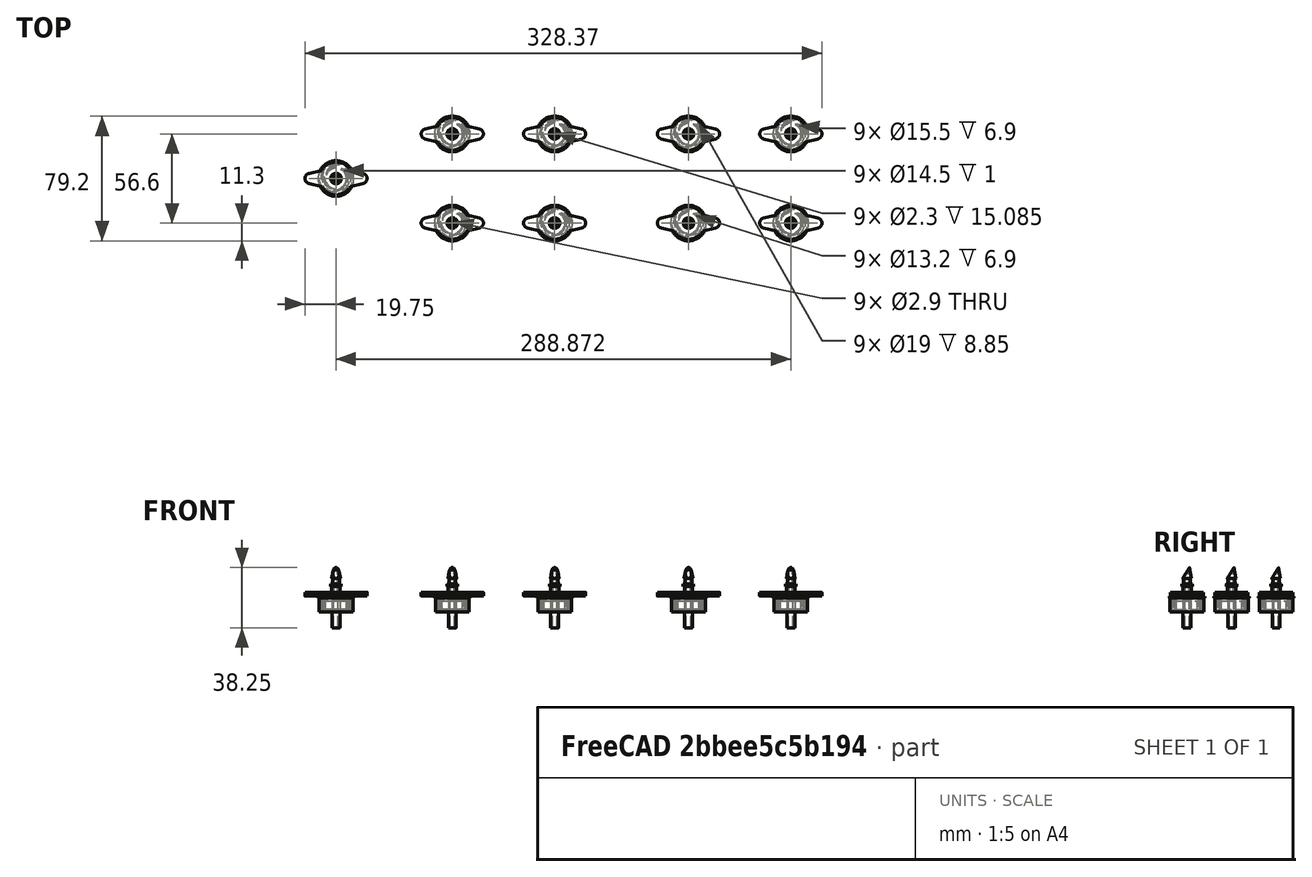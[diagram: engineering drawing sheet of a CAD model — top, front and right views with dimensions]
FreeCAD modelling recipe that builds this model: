
FCSTD DOCUMENT  (FreeCAD 1.1R38827 (Git))
Label: composit_stand3_dropper_fix_assembly
License: All rights reserved
LicenseURL: http://en.wikipedia.org/wiki/All_rights_reserved
objects: App::Link×10, PartDesign::CoordinateSystem×2, App::Part×2, Part::Compound×1, Part::FeaturePython×1, App::DocumentObjectGroup×1
note: 4 computed .brp shape members not serialized (recipe doc carries the construction recipe); baked Part::Feature solids carry a one-line shape summary decoded from their .brp
EXTERNAL_REF file=composit_stand3_dropper_fix_bottom_model.FCStd obj=Local_CS
EXTERNAL_REF file=composit_stand3_dropper_fix_bottom_model.FCStd obj=Body
EXTERNAL_REF file=composit_stand3_dropper_fix_top_model.FCStd obj=Local_CS
EXTERNAL_REF file=composit_stand3_dropper_fix_top_model.FCStd obj=Body
EXTERNAL_REF file=composit_stand3_dropper_fix_fixture_model.FCStd obj=Local_CS
EXTERNAL_REF file=composit_stand3_dropper_fix_fixture_model.FCStd obj=Body
EXTERNAL_REF file=composit_stand3_dropper_fix_cap_outer_model.FCStd obj=Local_CS
EXTERNAL_REF file=composit_stand3_dropper_fix_cap_outer_model.FCStd obj=Body
EXTERNAL_REF file=composit_stand3_dropper_fix_cap_inner_model.FCStd obj=Local_CS
EXTERNAL_REF file=composit_stand3_dropper_fix_cap_inner_model.FCStd obj=Body
EXTERNAL_REF file=composit_stand3_dropper_fix_cap_inner_model.FCStd obj=Local_CS001
EXTERNAL_REF file=composit_stand3_dropper_fix_cap_inner_model.FCStd obj=Body001
EXTERNAL_REF file=composit_stand3_dropper_fix_bottom_model.FCStd obj=Join
EXTERNAL_REF file=../dropper.FCStd obj=Body
EXTERNAL_REF file=../dropper.FCStd obj=Body001

FEATURE [PartDesign::CoordinateSystem] LCS_Origin
  AttacherType = Attacher::AttachEngine3D
FEATURE [App::Link] dropper_fix_bottom
  AttachedBy = #Local_CS
  AttachedTo = Parent Assembly#LCS_Origin
  LinkedObject = -> <external composit_stand3_dropper_fix_bottom_model.FCStd>#Body
  SolverId = Asm4EE
  expr: Placement = LCS_Origin.Placement * AttachmentOffset * composit_stand3_dropper_fix_bottom_model#Local_CS.Placement ^ -1
FEATURE [App::Link] dropper_fix_top
  AttachedBy = #Local_CS
  AttachedTo = dropper_fix_bottom#Local_CS
  LinkPlacement = pos=(0,-7e-16,6) rot=(-1,0,0;3.14159rad)
  LinkedObject = -> <external composit_stand3_dropper_fix_top_model.FCStd>#Body
  Placement = pos=(0,-7e-16,6) rot=(-1,0,0;3.14159rad)
  SolverId = Asm4EE
  expr: Placement = dropper_fix_bottom.Placement * composit_stand3_dropper_fix_bottom_model#Local_CS.Placement * AttachmentOffset * composit_stand3_dropper_fix_top_model#Local_CS.Placement ^ -1
FEATURE [App::Link] dropper_fix_fixture
  AttachedBy = #Local_CS
  AttachedTo = dropper_fix_bottom#Local_CS
  LinkPlacement = pos=(50,0,0) rot=(0,0,1;0rad)
  LinkedObject = -> <external composit_stand3_dropper_fix_fixture_model.FCStd>#Body
  Placement = pos=(50,0,0) rot=(0,0,1;0rad)
  SolverId = Asm4EE
  expr: Placement = dropper_fix_bottom.Placement * composit_stand3_dropper_fix_bottom_model#Local_CS.Placement * AttachmentOffset * composit_stand3_dropper_fix_fixture_model#Local_CS.Placement ^ -1
FEATURE [App::Link] cap_outer_dropper_fix
  AttachedBy = #Local_CS
  AttachedTo = Parent Assembly#LCS_Origin
  LinkedObject = -> <external composit_stand3_dropper_fix_cap_outer_model.FCStd>#Body
  SolverId = Asm4EE
  expr: Placement = LCS_Origin.Placement * AttachmentOffset * composit_stand3_dropper_fix_cap_outer_model#Local_CS.Placement ^ -1
FEATURE [App::Link] cap_inner_1
  AttachedBy = #Local_CS
  AttachedTo = cap_outer_dropper_fix#Local_CS
  LinkedObject = -> <external composit_stand3_dropper_fix_cap_inner_model.FCStd>#Body
  SolverId = Asm4EE
  expr: Placement = cap_outer_dropper_fix.Placement * composit_stand3_dropper_fix_cap_outer_model#Local_CS.Placement * AttachmentOffset * composit_stand3_dropper_fix_cap_inner_model#Local_CS.Placement ^ -1
FEATURE [App::Link] cap_inner_2
  AttachedBy = #Local_CS001
  AttachedTo = cap_outer_dropper_fix#Local_CS
  LinkedObject = -> <external composit_stand3_dropper_fix_cap_inner_model.FCStd>#Body001
  SolverId = Asm4EE
  expr: Placement = cap_outer_dropper_fix.Placement * composit_stand3_dropper_fix_cap_outer_model#Local_CS.Placement * AttachmentOffset * composit_stand3_dropper_fix_cap_inner_model#Local_CS001.Placement ^ -1
FEATURE [App::Link] Link001  label="Join"
  LinkedObject = -> <external composit_stand3_dropper_fix_bottom_model.FCStd>#Join
FEATURE [App::Link] Link002  label="Body"
  LinkedObject = -> <external ../dropper.FCStd>#Body
FEATURE [App::Link] Link003  label="Body001"
  LinkPlacement = pos=(0,0,2.5) rot=(0,0,1;0rad)
  LinkedObject = -> <external ../dropper.FCStd>#Body001
  Placement = pos=(0,0,2.5) rot=(0,0,1;0rad)
FEATURE [Part::Compound] Compound
  Links = -> [Link002,Link003]
  Placement = pos=(0,0,4) rot=(1,0,0;3.14159rad)
FEATURE [Part::FeaturePython] Populate  label="Populate Join with dropper"  # WARN: FeaturePython — macro-defined, semantics opaque (R4)
  Copying = 0
  ExposePlacement = false
  MarkerShape = 1
  MarkerSize = 0
  NumElements = 0
  Object = -> Compound
  OutputCompounding = 1
  PlacementsTo = -> Link001
  Referencing = 0
  Type = lattice2PopulateCopies.LatticePopulateCopies
  isLattice = 0
FEATURE [PartDesign::CoordinateSystem] base_LCS
  AttacherType = Attacher::AttachEngine3D
  AttachmentSupport = -> [XY_Plane001]
FEATURE [App::Part] Part  label="droppers"
  Group = -> [Link003,Link002,Link001,Compound,Populate,base_LCS]
  Origin = -> Origin001
FEATURE [App::DocumentObjectGroup] Parts
  Group = -> [Part]
FEATURE [App::Link] droppers  label="droppers001"
  AttachedBy = #base_LCS
  AttachedTo = Parent Assembly#LCS_Origin
  LinkedObject = -> Part
  SolverId = Asm4EE
  expr: Placement = LCS_Origin.Placement * AttachmentOffset * base_LCS.Placement ^ -1
FEATURE [App::Part] Assembly
  AssemblyType = Part::Link
  Group = -> [LCS_Origin,dropper_fix_bottom,dropper_fix_top,dropper_fix_fixture,cap_outer_dropper_fix,cap_inner_1,cap_inner_2,droppers]
  Origin = -> Origin
  Type = Assembly

RESOLVED EXTERNAL PARTS (link-assembly join: the EXTERNAL_REF files above that resolve inside this repo's crawl, each included once):
---- part ../dropper.FCStd = doc fcstd_03601a3bb068 ----
FCSTD DOCUMENT  (FreeCAD 1.1R38827 (Git))
Label: dropper
License: All rights reserved
LicenseURL: http://en.wikipedia.org/wiki/All_rights_reserved
objects: Sketcher::SketchObject×9, Part::FeaturePython×4, PartDesign::Revolution×3, PartDesign::Body×2, PartDesign::CoordinateSystem×1, Spreadsheet::Sheet×1, PartDesign::SubShapeBinder×1, PartDesign::Pad×1, PartDesign::Pocket×1, PartDesign::Groove×1, App::Part×1
note: 44 computed .brp shape members not serialized (recipe doc carries the construction recipe); baked Part::Feature solids carry a one-line shape summary decoded from their .brp

FEATURE [Sketcher::SketchObject] Sketch005
  ArcFitTolerance = 0
  AttachmentSupport = -> [YZ_Plane001]
  FullyConstrained = true
  MakeInternals = false
  MapMode = 5
  Placement = pos=(0,0,0) rot=(0.57735,0.57735,0.57735;2.0944rad)
  sketch-geometry (14):
    g0: LineSegment StartX=11.3 StartY=0 StartZ=0 EndX=11.3 EndY=1 EndZ=0
    g1: LineSegment StartX=11.3 StartY=1 StartZ=0 EndX=10.7 EndY=1 EndZ=0
    g2: LineSegment StartX=10.7 StartY=1 StartZ=0 EndX=10.7 EndY=9.9 EndZ=0
    g3: LineSegment StartX=10.7 StartY=9.9 StartZ=0 EndX=6.6 EndY=9.9 EndZ=0
    g4: LineSegment StartX=6.6 StartY=9.9 StartZ=0 EndX=6.6 EndY=3 EndZ=0
    g5: LineSegment StartX=6.6 StartY=3 StartZ=0 EndX=2.5 EndY=3 EndZ=0
    g6: LineSegment StartX=2.5 StartY=3 StartZ=0 EndX=2.5 EndY=20 EndZ=0
    g7: LineSegment StartX=2.5 StartY=20 StartZ=0 EndX=1.45 EndY=20 EndZ=0
    g8: LineSegment StartX=1.45 StartY=20 StartZ=0 EndX=1.45 EndY=2.5 EndZ=0
    g9: LineSegment StartX=1.45 StartY=2.5 StartZ=0 EndX=7 EndY=-0.6 EndZ=0
    g10: LineSegment StartX=7 StartY=-0.6 StartZ=0 EndX=7 EndY=8.85 EndZ=0
    g11: LineSegment StartX=7 StartY=8.85 StartZ=0 EndX=9.5 EndY=8.85 EndZ=0
    g12: LineSegment StartX=9.5 StartY=8.85 StartZ=0 EndX=9.5 EndY=0 EndZ=0
    g13: LineSegment StartX=9.5 StartY=0 StartZ=0 EndX=11.3 EndY=0 EndZ=0
  constraints (43):
    c: PointOnObject(g0,g-1)
    c: Vertical(g0)
    c: Coincident(g0,g1)
    c: Horizontal(g1)
    c: Coincident(g1,g2)
    c: Vertical(g2)
    c: Coincident(g2,g3)
    c: Horizontal(g3)
    c: Coincident(g3,g4)
    c: Vertical(g4)
    c: Coincident(g4,g5)
    c: Coincident(g5,g6)
    c: Vertical(g6)
    c: Coincident(g6,g7)
    c: Horizontal(g7)
    c: Coincident(g7,g8)
    c: Vertical(g8)
    c: Coincident(g8,g9)
    c: Coincident(g9,g10)
    c: Vertical(g10)
    c: Coincident(g10,g11)
    c: Horizontal(g11)
    c: Coincident(g11,g12)
    c: Vertical(g12)
    c: Coincident(g12,g13)
    c: Coincident(g13,g0)
    c: Horizontal(g13)
    c: DistanceX(g0) = 11.3  'outer_r'
    c: DistanceY(g0) = 1
    c: DistanceY(g2) = 9.9
    c: DistanceX(g1,g0) = 0.6
    c: DistanceX(g3,g2) = 4.1
    c: DistanceY(g4,g3) = 6.9
    c: DistanceX(g6) = 2.5
    c: DistanceX(g7) = 1.45
    c: DistanceY(g9,g3) = 10.5
    c: DistanceX(g12,g0) = 1.8
    c: DistanceY(g11) = 8.85
    c: DistanceX(g9) = 7
    c: DistanceY(g9,g6) = 20.6
    c: Horizontal(g5)
    c: DistanceY(g8,g5) = 0.5
    c: DistanceY(g7) = 20
FEATURE [PartDesign::Revolution] Revolution002
  Angle = 360
  Angle2 = 60
  Axis = (0,0,1)
  Base = (0,0,0)
  Placement = pos=(0,0,0) rot=(1,1,1;2.0944rad)
  Profile = -> Sketch005
  ReferenceAxis = -> Sketch005 [V_Axis]
  Reversed = true
  Suppressed = false
  Type = 0
FEATURE [Sketcher::SketchObject] Sketch006
  ArcFitTolerance = 0
  AttachmentSupport = -> [YZ_Plane001]
  FullyConstrained = true
  MakeInternals = false
  MapMode = 5
  Placement = pos=(0,0,0) rot=(0.57735,0.57735,0.57735;2.0944rad)
  expr: Constraints[27] = Sketch005.Constraints.outer_r
  expr: Constraints[28] = Sketch005.Constraints[28]
  expr: Constraints[29] = Sketch005.Constraints[29]
  expr: Constraints[30] = Sketch005.Constraints[30]
  expr: Constraints[31] = Sketch005.Constraints[31]
  expr: Constraints[32] = Sketch005.Constraints[32]
  expr: Constraints[33] = Sketch005.Constraints[33]
  expr: Constraints[34] = Sketch005.Constraints[34]
  expr: Constraints[35] = Sketch005.Constraints[35]
  expr: Constraints[36] = Sketch005.Constraints[36]
  expr: Constraints[37] = Sketch005.Constraints[37]
  expr: Constraints[38] = Sketch005.Constraints[38]
  expr: Constraints[39] = Sketch005.Constraints[39]
  expr: Constraints[41] = Sketch005.Constraints[41]
  expr: Constraints[69] = Sketch005.Constraints.outer_r
  expr: Constraints[70] = Sketch005.Constraints[28]
  expr: Constraints[71] = Sketch005.Constraints[29]
  expr: Constraints[72] = Sketch005.Constraints[30]
  expr: Constraints[73] = Sketch005.Constraints[31]
  expr: Constraints[74] = Sketch005.Constraints[32]
  expr: Constraints[75] = Sketch005.Constraints[33]
  expr: Constraints[76] = Sketch005.Constraints[34]
  expr: Constraints[77] = Sketch005.Constraints[35]
  expr: Constraints[78] = Sketch005.Constraints[36]
  expr: Constraints[79] = Sketch005.Constraints[37]
  expr: Constraints[80] = Sketch005.Constraints[38]
  expr: Constraints[81] = Sketch005.Constraints[39]
  expr: Constraints[83] = Sketch005.Constraints[41]
  sketch-geometry (32):
    g0: LineSegment [constr] StartX=11.3 StartY=0 StartZ=0 EndX=11.3 EndY=1 EndZ=0
    g1: LineSegment [constr] StartX=11.3 StartY=1 StartZ=0 EndX=10.7 EndY=1 EndZ=0
    g2: LineSegment [constr] StartX=10.7 StartY=1 StartZ=0 EndX=10.7 EndY=9.9 EndZ=0
    g3: LineSegment [constr] StartX=10.7 StartY=9.9 StartZ=0 EndX=6.6 EndY=9.9 EndZ=0
    g4: LineSegment StartX=6.6 StartY=9.9 StartZ=0 EndX=6.6 EndY=3 EndZ=0
    g5: LineSegment StartX=6.6 StartY=3 StartZ=0 EndX=2.5 EndY=3 EndZ=0
    g6: LineSegment [constr] StartX=2.5 StartY=3 StartZ=0 EndX=2.5 EndY=20 EndZ=0
    g7: LineSegment [constr] StartX=2.5 StartY=20 StartZ=0 EndX=1.45 EndY=20 EndZ=0
    g8: LineSegment [constr] StartX=1.45 StartY=20 StartZ=0 EndX=1.45 EndY=2.5 EndZ=0
    g9: LineSegment [constr] StartX=1.45 StartY=2.5 StartZ=0 EndX=7 EndY=-0.6 EndZ=0
    g10: LineSegment [constr] StartX=7 StartY=-0.6 StartZ=0 EndX=7 EndY=8.85 EndZ=0
    g11: LineSegment [constr] StartX=7 StartY=8.85 StartZ=0 EndX=9.5 EndY=8.85 EndZ=0
    g12: LineSegment [constr] StartX=9.5 StartY=8.85 StartZ=0 EndX=9.5 EndY=0 EndZ=0
    g13: LineSegment [constr] StartX=9.5 StartY=0 StartZ=0 EndX=11.3 EndY=0 EndZ=0
    g14: LineSegment [constr] StartX=11.3 StartY=0 StartZ=0 EndX=11.3 EndY=1 EndZ=0
    g15: LineSegment [constr] StartX=11.3 StartY=1 StartZ=0 EndX=10.7 EndY=1 EndZ=0
    g16: LineSegment [constr] StartX=10.7 StartY=1 StartZ=0 EndX=10.7 EndY=9.9 EndZ=0
    g17: LineSegment [constr] StartX=10.7 StartY=9.9 StartZ=0 EndX=6.6 EndY=9.9 EndZ=0
    g18: LineSegment [constr] StartX=6.6 StartY=9.9 StartZ=0 EndX=6.6 EndY=3 EndZ=0
    g19: LineSegment [constr] StartX=6.6 StartY=3 StartZ=0 EndX=2.5 EndY=3 EndZ=0
    g20: LineSegment [constr] StartX=2.5 StartY=3 StartZ=0 EndX=2.5 EndY=20 EndZ=0
    g21: LineSegment [constr] StartX=2.5 StartY=20 StartZ=0 EndX=1.45 EndY=20 EndZ=0
    g22: LineSegment [constr] StartX=1.45 StartY=20 StartZ=0 EndX=1.45 EndY=2.5 EndZ=0
    g23: LineSegment [constr] StartX=1.45 StartY=2.5 StartZ=0 EndX=7 EndY=-0.6 EndZ=0
    g24: LineSegment [constr] StartX=7 StartY=-0.6 StartZ=0 EndX=7 EndY=8.85 EndZ=0
    g25: LineSegment [constr] StartX=7 StartY=8.85 StartZ=0 EndX=9.5 EndY=8.85 EndZ=0
    g26: LineSegment [constr] StartX=9.5 StartY=8.85 StartZ=0 EndX=9.5 EndY=0 EndZ=0
    g27: LineSegment [constr] StartX=9.5 StartY=0 StartZ=0 EndX=11.3 EndY=0 EndZ=0
    g28: LineSegment StartX=2.5 StartY=3 StartZ=0 EndX=2.04763 EndY=3 EndZ=0
    g29: LineSegment StartX=2.04763 StartY=3 StartZ=0 EndX=2.04763 EndY=12.6758 EndZ=0
    g30: LineSegment StartX=2.04763 StartY=12.6758 StartZ=0 EndX=6.6 EndY=9.9 EndZ=0
    g31: GeomPoint [constr] X=2.5 Y=12.4 Z=0
  constraints (94):
    c: PointOnObject(g0,g-1)
    c: Vertical(g0)
    c: Coincident(g0,g1)
    c: Horizontal(g1)
    c: Coincident(g1,g2)
    c: Vertical(g2)
    c: Coincident(g2,g3)
    c: Horizontal(g3)
    c: Coincident(g3,g4)
    c: Vertical(g4)
    c: Coincident(g4,g5)
    c: Coincident(g5,g6)
    c: Vertical(g6)
    c: Coincident(g6,g7)
    c: Horizontal(g7)
    c: Coincident(g7,g8)
    c: Vertical(g8)
    c: Coincident(g8,g9)
    c: Coincident(g9,g10)
    c: Vertical(g10)
    c: Coincident(g10,g11)
    c: Horizontal(g11)
    c: Coincident(g11,g12)
    c: Vertical(g12)
    c: Coincident(g12,g13)
    c: Coincident(g13,g0)
    c: Horizontal(g13)
    c: DistanceX(g0) = 11.3
    c: DistanceY(g0) = 1
    c: DistanceY(g2) = 9.9
    c: DistanceX(g1,g0) = 0.6
    c: DistanceX(g3,g2) = 4.1
    c: DistanceY(g4,g3) = 6.9
    c: DistanceX(g6) = 2.5
    c: DistanceX(g7) = 1.45
    c: DistanceY(g9,g3) = 10.5
    c: DistanceX(g12,g0) = 1.8
    c: DistanceY(g11) = 8.85
    c: DistanceX(g9) = 7
    c: DistanceY(g9,g6) = 20.6
    c: Horizontal(g5)
    c: DistanceY(g8,g5) = 0.5
    c: PointOnObject(g14,g-1)
    c: Vertical(g14)
    c: Coincident(g14,g15)
    c: Horizontal(g15)
    c: Coincident(g15,g16)
    c: Vertical(g16)
    c: Coincident(g16,g17)
    c: Horizontal(g17)
    c: Coincident(g17,g18)
    c: Vertical(g18)
    c: Coincident(g18,g19)
    c: Coincident(g19,g20)
    c: Vertical(g20)
    c: Coincident(g20,g21)
    c: Horizontal(g21)
    c: Coincident(g21,g22)
    c: Vertical(g22)
    c: Coincident(g22,g23)
    c: Coincident(g23,g24)
    c: Vertical(g24)
    c: Coincident(g24,g25)
    c: Horizontal(g25)
    c: Coincident(g25,g26)
    c: Vertical(g26)
    c: Coincident(g26,g27)
    c: Coincident(g27,g14)
    c: Horizontal(g27)
    c: DistanceX(g14) = 11.3
    c: DistanceY(g14) = 1
    c: DistanceY(g16) = 9.9
    c: DistanceX(g15,g14) = 0.6
    c: DistanceX(g17,g16) = 4.1
    c: DistanceY(g18,g17) = 6.9
    c: DistanceX(g20) = 2.5
    c: DistanceX(g21) = 1.45
    c: DistanceY(g23,g17) = 10.5
    c: DistanceX(g26,g14) = 1.8
    c: DistanceY(g25) = 8.85
    c: DistanceX(g23) = 7
    c: DistanceY(g23,g20) = 20.6
    c: Horizontal(g19)
    c: DistanceY(g22,g19) = 0.5
    c: Coincident(g28,g5)
    c: Horizontal(g28)
    c: Coincident(g29,g28)
    c: Vertical(g29)
    c: Coincident(g30,g29)
    c: Coincident(g30,g4)
    c: PointOnObject(g31,g30)
    c: PointOnObject(g31,g6)
    c: DistanceY(g4,g31) = 2.5
    c: DistanceX(g29,g31) = 0.452366
FEATURE [PartDesign::Body] Body001
  AllowCompound = false
  Group = -> [Sketch005,Revolution002,Sketch006]
  Origin = -> Origin001
  Placement = pos=(0,0,2.5) rot=(0,0,1;0rad)
  Tip = -> Revolution002
FEATURE [Sketcher::SketchObject] Sketch007  label="base"
  ArcFitTolerance = 0
  FullyConstrained = true
  MakeInternals = false
  expr: .Constraints.r = Sketch005.Constraints.outer_r + 0.5 mm
  sketch-geometry (1):
    g0: Circle CenterX=0 CenterY=0 CenterZ=0 NormalX=0 NormalY=0 NormalZ=1 AngleXU=0 Radius=11.8
  constraints (2):
    c: Coincident(g0,g-1)
    c: Radius(g0) = 11.8  'r'
FEATURE [Sketcher::SketchObject] Sketch002
  ArcFitTolerance = 0
  AttachmentSupport = -> [YZ_Plane]
  FullyConstrained = true
  MakeInternals = false
  MapMode = 5
  Placement = pos=(0,0,0) rot=(0.57735,0.57735,0.57735;2.0944rad)
  expr: Constraints[18] = Sketch001.Constraints[18]
  expr: Constraints[19] = Sketch001.Constraints[19]
  expr: Constraints[20] = Sketch001.Constraints[20]
  expr: Constraints[21] = Sketch001.Constraints[21]
  expr: Constraints[22] = Sketch001.Constraints[22]
  expr: Constraints[23] = Sketch001.Constraints[23]
  expr: Constraints[24] = Sketch001.Constraints[24]
  expr: Constraints[25] = Sketch001.Constraints[25]
  expr: Constraints[27] = Sketch001.Constraints[27]
  sketch-geometry (13):
    g0: LineSegment [constr] StartX=1.15 StartY=0 StartZ=0 EndX=1.15 EndY=-18.1612 EndZ=0
    g1: LineSegment StartX=1.15 StartY=-18.1612 StartZ=0 EndX=2.765 EndY=-8.77 EndZ=0
    g2: LineSegment [constr] StartX=2.765 StartY=-8.77 StartZ=0 EndX=2.2 EndY=-8.77 EndZ=0
    g3: LineSegment [constr] StartX=2.2 StartY=-8.77 StartZ=0 EndX=2.2 EndY=-5.32 EndZ=0
    g4: LineSegment [constr] StartX=2.2 StartY=-5.32 StartZ=0 EndX=3.35 EndY=-5.32 EndZ=0
    g5: LineSegment [constr] StartX=3.35 StartY=-5.32 StartZ=0 EndX=3.35 EndY=-3.66 EndZ=0
    g6: LineSegment [constr] StartX=3.35 StartY=-3.66 StartZ=0 EndX=2.65 EndY=-3.66 EndZ=0
    g7: LineSegment [constr] StartX=2.65 StartY=-3.66 StartZ=0 EndX=2.65 EndY=0 EndZ=0
    g8: LineSegment [constr] StartX=2.65 StartY=0 StartZ=0 EndX=1.15 EndY=0 EndZ=0
    g9: GeomPoint [constr] X=-2.765 Y=-8.77 Z=0
    g10: GeomPoint [constr] X=-2.765 Y=-8.77 Z=0
    g11: LineSegment StartX=1.15 StartY=-18.1612 StartZ=0 EndX=-3.0574 EndY=-18.1612 EndZ=0
    g12: LineSegment StartX=-3.0574 StartY=-18.1612 StartZ=0 EndX=2.765 EndY=-8.77 EndZ=0
  constraints (34):
    c: PointOnObject(g0,g-1)
    c: Vertical(g0)
    c: Coincident(g0,g1)
    c: Coincident(g1,g2)
    c: Horizontal(g2)
    c: Coincident(g2,g3)
    c: Vertical(g3)
    c: Coincident(g3,g4)
    c: Horizontal(g4)
    c: Coincident(g4,g5)
    c: Vertical(g5)
    c: Coincident(g5,g6)
    c: Horizontal(g6)
    c: Coincident(g6,g7)
    c: PointOnObject(g7,g-1)
    c: Vertical(g7)
    c: Coincident(g7,g8)
    c: Coincident(g8,g0)
    c: DistanceY(g2,g3) = 3.45
    c: DistanceY(g4,g5) = 1.66
    c: DistanceY(g6,g7) = 3.66
    c: DistanceX(g2) = 2.2
    c: DistanceX(g4) = 3.35
    c: DistanceX(g0) = 1.15
    c: DistanceX(g7) = 2.65
    c: DistanceX(g1) = 2.765
    c: Symmetric(g9,g1,g-2)
    c: Distance(g9,g1) = 5.45
    c: Symmetric(g10,g1,g-2)
    c: Coincident(g11,g1)
    c: Horizontal(g11)
    c: Coincident(g12,g11)
    c: Coincident(g12,g1)
    c: Distance(g9,g12) = 4.7
FEATURE [Sketcher::SketchObject] Sketch001
  ArcFitTolerance = 0
  AttachmentSupport = -> [XZ_Plane]
  FullyConstrained = true
  MakeInternals = false
  MapMode = 5
  Placement = pos=(0,0,0) rot=(1,0,0;1.5708rad)
  sketch-geometry (10):
    g0: LineSegment StartX=1.15 StartY=0 StartZ=0 EndX=1.15 EndY=-18.1612 EndZ=0
    g1: LineSegment StartX=1.15 StartY=-18.1612 StartZ=0 EndX=2.765 EndY=-8.77 EndZ=0
    g2: LineSegment StartX=2.765 StartY=-8.77 StartZ=0 EndX=2.2 EndY=-8.77 EndZ=0
    g3: LineSegment StartX=2.2 StartY=-8.77 StartZ=0 EndX=2.2 EndY=-5.32 EndZ=0
    g4: LineSegment StartX=2.2 StartY=-5.32 StartZ=0 EndX=3.35 EndY=-5.32 EndZ=0
    g5: LineSegment StartX=3.35 StartY=-5.32 StartZ=0 EndX=3.35 EndY=-3.66 EndZ=0
    g6: LineSegment StartX=3.35 StartY=-3.66 StartZ=0 EndX=2.65 EndY=-3.66 EndZ=0
    g7: LineSegment StartX=2.65 StartY=-3.66 StartZ=0 EndX=2.65 EndY=0 EndZ=0
    g8: LineSegment StartX=2.65 StartY=0 StartZ=0 EndX=1.15 EndY=0 EndZ=0
    g9: GeomPoint [constr] X=-2.765 Y=-8.77 Z=0
  constraints (28):
    c: PointOnObject(g0,g-1)
    c: Vertical(g0)
    c: Coincident(g0,g1)
    c: Coincident(g1,g2)
    c: Horizontal(g2)
    c: Coincident(g2,g3)
    c: Vertical(g3)
    c: Coincident(g3,g4)
    c: Horizontal(g4)
    c: Coincident(g4,g5)
    c: Vertical(g5)
    c: Coincident(g5,g6)
    c: Horizontal(g6)
    c: Coincident(g6,g7)
    c: PointOnObject(g7,g-1)
    c: Vertical(g7)
    c: Coincident(g7,g8)
    c: Coincident(g8,g0)
    c: DistanceY(g2,g3) = 3.45
    c: DistanceY(g4,g5) = 1.66
    c: DistanceY(g6,g7) = 3.66
    c: DistanceX(g2) = 2.2
    c: DistanceX(g4) = 3.35
    c: DistanceX(g0) = 1.15
    c: DistanceX(g7) = 2.65
    c: DistanceX(g1) = 2.765
    c: Symmetric(g9,g1,g-2)
    c: Distance(g9,g1) = 5.45
FEATURE [Sketcher::SketchObject] Sketch  label="fix_sketch"
  ArcFitTolerance = 0
  AttachmentSupport = -> [XY_Plane]
  FullyConstrained = true
  MakeInternals = false
  MapMode = 5
  sketch-geometry (5):
    g0: ArcOfCircle CenterX=0 CenterY=0 CenterZ=0 NormalX=0 NormalY=0 NormalZ=1 AngleXU=0 Radius=10.5 StartAngle=0.496317 EndAngle=1.5708
    g1: ArcOfCircle CenterX=16.5 CenterY=0 CenterZ=0 NormalX=0 NormalY=0 NormalZ=1 AngleXU=0 Radius=3.25 StartAngle=0 EndAngle=1.34547
    g2: LineSegment StartX=17.2261 StartY=3.16784 StartZ=0 EndX=9.23309 EndY=5 EndZ=0
    g3: GeomPoint [constr] X=-19.75 Y=0 Z=0
    g4: GeomPoint [constr] X=0 Y=-10.5 Z=0
  constraints (14):
    c: PointOnObject(g0,g-2)
    c: PointOnObject(g1,g-1)
    c: PointOnObject(g1,g-1)
    c: Coincident(g2,g0)
    c: Tangent(g2,g1) = -1.5708
    c: Diameter(g0) = 21
    c: DistanceX(g1) = 19.75
    c: DistanceY(g0) = 5
    c: Diameter(g1) = 6.5
    c: Coincident(g0,g-1)
    c: Symmetric(g3,g1,g-2)
    c: DistanceX(g3,g1) = 39.5  'length'
    c: Symmetric(g4,g0,g-1)
    c: DistanceY(g4,g0) = 21  'width'
FEATURE [Sketcher::SketchObject] Sketch004
  ArcFitTolerance = 0
  AttachmentSupport = -> [YZ_Plane]
  FullyConstrained = true
  MakeInternals = false
  MapMode = 5
  Placement = pos=(0,0,0) rot=(0.57735,0.57735,0.57735;2.0944rad)
  expr: Constraints[3] = Sketch003.Constraints[9]
  sketch-geometry (6):
    g0: LineSegment StartX=7.75 StartY=10.9 StartZ=0 EndX=0 EndY=10.9 EndZ=0
    g1: LineSegment StartX=0 StartY=10.9 StartZ=0 EndX=0 EndY=1.5 EndZ=0
    g2: LineSegment StartX=0 StartY=1.5 StartZ=0 EndX=7.25 EndY=1.5 EndZ=0
    g3: LineSegment StartX=7.25 StartY=1.5 StartZ=0 EndX=7.25 EndY=2.5 EndZ=0
    g4: LineSegment StartX=7.25 StartY=2.5 StartZ=0 EndX=7.75 EndY=4 EndZ=0
    g5: LineSegment StartX=7.75 StartY=4 StartZ=0 EndX=7.75 EndY=10.9 EndZ=0
  constraints (18):
    c: Coincident(g0,g1)
    c: Horizontal(g0)
    c: Vertical(g1)
    c: DistanceY(g0) = 10.9
    c: Horizontal(g2)
    c: Coincident(g2,g3)
    c: Vertical(g3)
    c: Coincident(g3,g4)
    c: Coincident(g4,g5)
    c: Vertical(g5)
    c: Coincident(g0,g5)
    c: Coincident(g1,g2)
    c: DistanceY(g1,g0) = 9.4
    c: DistanceX(g0) = 7.75
    c: DistanceY(g2,g3) = 1
    c: DistanceY(g3,g4) = 1.5
    c: DistanceX(g2,g4) = 0.5
    c: Vertical(g1,g-1)
FEATURE [Sketcher::SketchObject] Sketch003
  ArcFitTolerance = 0
  AttachmentSupport = -> [YZ_Plane]
  FullyConstrained = true
  MakeInternals = false
  MapMode = 5
  Placement = pos=(0,0,0) rot=(0.57735,0.57735,0.57735;2.0944rad)
  sketch-geometry (4):
    g0: LineSegment StartX=0 StartY=0 StartZ=0 EndX=8.825 EndY=0 EndZ=0
    g1: LineSegment StartX=8.825 StartY=0 StartZ=0 EndX=8.825 EndY=10.9 EndZ=0
    g2: LineSegment StartX=8.825 StartY=10.9 StartZ=0 EndX=0 EndY=10.9 EndZ=0
    g3: LineSegment StartX=0 StartY=10.9 StartZ=0 EndX=0 EndY=0 EndZ=0
  constraints (11):
    c: Coincident(g0,g1)
    c: Coincident(g1,g2)
    c: Coincident(g2,g3)
    c: Coincident(g3,g0)
    c: Horizontal(g0)
    c: Horizontal(g2)
    c: Vertical(g1)
    c: Vertical(g3)
    c: Coincident(g0,g-1)
    c: DistanceY(g2) = 10.9
    c: DistanceX(g0) = 8.825
FEATURE [PartDesign::CoordinateSystem] LCS_0
  AttacherType = Attacher::AttachEngine3D
  AttachmentOffset = pos=(0,0,2.45) rot=(0,0,1;0rad)
  AttachmentSupport = -> [X_Axis002]
  MapMode = 2
  Placement = pos=(0,0,2.45) rot=(0,0,1;0rad)
FEATURE [Spreadsheet::Sheet] Spreadsheet  label="Properties"
  cells = B2(top_d)==22.6 mm; C2(bot_d)==21 mm; D2(top_height)==20 mm; E2(bot_base_height)==2.4 mm; F2(total_height)==22.4 mm; G2(total_width)==38.9 mm
FEATURE [Part::FeaturePython] Mirror  label="Mirror of Sketch"  # WARN: FeaturePython — macro-defined, semantics opaque (R4)
  ExposePlacement = false
  FlipX = true
  FlipY = false
  FlipZ = false
  MarkerShape = 1
  MarkerSize = 0
  NumElements = 0
  Object = -> Sketch
  ObjectTraversal = 0
  Type = lattice2Mirror.LatticeMirror
  isLattice = 0
FEATURE [Part::FeaturePython] Mirror001  label="Mirror001 of Mirror of Sketch"  # WARN: FeaturePython — macro-defined, semantics opaque (R4)
  ExposePlacement = false
  FlipX = false
  FlipY = true
  FlipZ = false
  MarkerShape = 1
  MarkerSize = 0
  NumElements = 0
  Object = -> Mirror
  ObjectTraversal = 0
  Type = lattice2Mirror.LatticeMirror
  isLattice = 0
FEATURE [Part::FeaturePython] Mirror002  label="Mirror002 of Mirror001 of Mirror of Sketch"  # WARN: FeaturePython — macro-defined, semantics opaque (R4)
  ExposePlacement = false
  FlipX = true
  FlipY = false
  FlipZ = false
  MarkerShape = 1
  MarkerSize = 0
  NumElements = 0
  Object = -> Mirror001
  ObjectTraversal = 0
  Type = lattice2Mirror.LatticeMirror
  isLattice = 0
FEATURE [PartDesign::SubShapeBinder] Binder
  BindCopyOnChange = 0
  BindMode = 0
  ClaimChildren = true
  Context = -> Part [Body.Binder.]
  Fuse = false
  MakeFace = true
  OffsetFill = false
  OffsetIntersection = false
  OffsetJoinType = 0
  OffsetOpenResult = false
  PartialLoad = false
  Relative = true
  Support = -> [Connect]
  _Version = 2
FEATURE [PartDesign::Pad] Pad
  Direction = (0,0,1)
  Length = 2.45
  Length2 = 10
  Profile = -> Binder
  Suppressed = false
  Type = 0
FEATURE [PartDesign::Revolution] Revolution
  Angle = 360
  Angle2 = 60
  Axis = (0,2e-16,1)
  Base = (0,0,0)
  BaseFeature = -> Pad
  Profile = -> Sketch001
  ReferenceAxis = -> Sketch001 [V_Axis]
  Reversed = true
  Suppressed = false
  Type = 0
FEATURE [PartDesign::Pocket] Pocket
  BaseFeature = -> Revolution
  Direction = (-1,0,0)
  Length = 5
  Length2 = 5
  Midplane = true
  Profile = -> Sketch002
  ReferenceAxis = -> Sketch002 [N_Axis]
  Suppressed = false
  Type = 1
FEATURE [PartDesign::Revolution] Revolution001
  Angle = 360
  Angle2 = 60
  Axis = (0,0,1)
  Base = (0,0,0)
  BaseFeature = -> Pocket
  Profile = -> Sketch003
  ReferenceAxis = -> Sketch003 [V_Axis]
  Reversed = true
  Suppressed = false
  Type = 0
FEATURE [PartDesign::Groove] Groove
  Angle = 360
  Angle2 = 60
  Axis = (0,0,1)
  Base = (0,0,0)
  BaseFeature = -> Revolution001
  Profile = -> Sketch004
  ReferenceAxis = -> Sketch004 [V_Axis]
  Suppressed = false
  Type = 0
FEATURE [Sketcher::SketchObject] Sketch008  label="feed"
  ArcFitTolerance = 0
  AttachmentSupport = -> [XY_Plane]
  FullyConstrained = true
  MakeInternals = false
  MapMode = 5
  sketch-geometry (1):
    g0: Circle CenterX=0 CenterY=0 CenterZ=0 NormalX=0 NormalY=0 NormalZ=1 AngleXU=0 Radius=4
  constraints (2):
    c: Coincident(g0,g-1)
    c: Diameter(g0) = 8
FEATURE [PartDesign::Body] Body
  AllowCompound = false
  Group = -> [Sketch,Pad,Sketch001,Revolution,Sketch002,Pocket,Sketch003,Sketch004,Revolution001,Groove,Sketch008,Binder]
  Origin = -> Origin
  Tip = -> Groove
FEATURE [App::Part] Part  label="dropper"
  Group = -> [LCS_0,Body001,Body]
  Origin = -> Origin002
FEATURE [Part::FeaturePython] Connect  label="fix"  # WARN: FeaturePython — macro-defined, semantics opaque (R4)
  Objects = -> [Sketch,Mirror002,Mirror001,Mirror]
  Tolerance = 0
---- part composit_stand3_dropper_fix_bottom_model.FCStd = doc fcstd_e59e662397be ----
FCSTD DOCUMENT  (FreeCAD 1.1R38827 (Git))
Label: composit_stand3_dropper_fix_bottom_model
License: All rights reserved
LicenseURL: http://en.wikipedia.org/wiki/All_rights_reserved
objects: Part::FeaturePython×9, PartDesign::SubShapeBinder×6, App::Link×4, PartDesign::Pad×3, PartDesign::Body×2, Part::Feature×2, Part::Mirroring×1, Part::Compound×1, Part::MultiFuse×1, PartDesign::Boolean×1, PartDesign::CoordinateSystem×1
note: 34 computed .brp shape members not serialized (recipe doc carries the construction recipe); baked Part::Feature solids carry a one-line shape summary decoded from their .brp
EXTERNAL_REF file=composit_stand3_dropper_fix_main.FCStd obj=Sketch
EXTERNAL_REF file=../dropper.FCStd obj=Sketch007
EXTERNAL_REF file=../dropper.FCStd obj=Part
EXTERNAL_REF file=composit_stand3_dropper_fix_main.FCStd obj=Populate
EXTERNAL_REF file=composit_stand3_dropper_fix_main.FCStd obj=Join
EXTERNAL_REF file=composit_stand3_main.FCStd obj=Cylinder
EXTERNAL_REF file=composit_stand3_dropper_fix_main.FCStd obj=Cylinder

FEATURE [PartDesign::SubShapeBinder] Binder
  BindCopyOnChange = 0
  BindMode = 0
  ClaimChildren = true
  Fuse = false
  MakeFace = true
  OffsetFill = false
  OffsetIntersection = false
  OffsetJoinType = 0
  OffsetOpenResult = false
  PartialLoad = false
  Relative = false
  Support = -> [<external composit_stand3_dropper_fix_main.FCStd>#Sketch]
  _Version = 2
FEATURE [Part::Mirroring] Part__Mirroring  label="Binder (Mirror #1)"
  Base = (0,0,0)
  Normal = (0,1,0)
  Source = -> Binder
FEATURE [Part::FeaturePython] Connect  # WARN: FeaturePython — macro-defined, semantics opaque (R4)
  Objects = -> [Binder,Part__Mirroring]
  Tolerance = 0
FEATURE [PartDesign::SubShapeBinder] Binder001
  BindCopyOnChange = 0
  BindMode = 0
  ClaimChildren = true
  Context = -> Body [Binder001.]
  Fuse = false
  MakeFace = true
  OffsetFill = false
  OffsetIntersection = false
  OffsetJoinType = 0
  OffsetOpenResult = false
  PartialLoad = false
  Relative = false
  Support = -> [Connect]
  _Version = 2
FEATURE [PartDesign::Pad] Pad
  Direction = (0,0,1)
  Length = 3
  Length2 = 10
  Profile = -> Binder001
  Suppressed = false
  Type = 0
FEATURE [PartDesign::SubShapeBinder] Binder002
  BindCopyOnChange = 0
  BindMode = 0
  ClaimChildren = true
  Fuse = false
  MakeFace = true
  OffsetFill = false
  OffsetIntersection = false
  OffsetJoinType = 0
  OffsetOpenResult = false
  PartialLoad = false
  Relative = false
  Support = -> [<external ../dropper.FCStd>#Sketch007]
  _Version = 2
  expr: Support = dropper#<<base>>._self
FEATURE [PartDesign::SubShapeBinder] Binder003
  BindCopyOnChange = 0
  BindMode = 0
  ClaimChildren = true
  Fuse = false
  MakeFace = true
  OffsetFill = false
  OffsetIntersection = false
  OffsetJoinType = 0
  OffsetOpenResult = false
  PartialLoad = false
  Relative = false
  Support = -> [<external ../dropper.FCStd>#Part[Body.Binder.Connect.]]
  _Version = 2
FEATURE [Part::Compound] Compound
  Links = -> [Binder002,Binder003]
FEATURE [Part::FeaturePython] FuseCompound  # WARN: FeaturePython — macro-defined, semantics opaque (R4)
  Base = -> Compound
  Refine = true
  recomputeQuota = -1
FEATURE [PartDesign::SubShapeBinder] Binder004
  BindCopyOnChange = 0
  BindMode = 0
  ClaimChildren = true
  Context = -> Body001 [Binder004.]
  Fuse = false
  MakeFace = true
  OffsetFill = false
  OffsetIntersection = false
  OffsetJoinType = 0
  OffsetOpenResult = false
  PartialLoad = false
  Relative = false
  Support = -> [Binder002]
  _Version = 2
FEATURE [PartDesign::SubShapeBinder] Binder005
  BindCopyOnChange = 0
  BindMode = 0
  ClaimChildren = true
  Context = -> Body001 [Binder005.]
  Fuse = false
  MakeFace = true
  OffsetFill = false
  OffsetIntersection = false
  OffsetJoinType = 0
  OffsetOpenResult = false
  PartialLoad = false
  Placement = pos=(0,0,1.5) rot=(0,0,1;0rad)
  Relative = false
  Support = -> [FuseCompound]
  _Version = 2
FEATURE [PartDesign::Pad] Pad001
  Direction = (0,0,1)
  Length = 10
  Length2 = 10
  Profile = -> Binder004
  Suppressed = false
  Type = 0
FEATURE [PartDesign::Pad] Pad002
  BaseFeature = -> Pad001
  Direction = (0,0,1)
  Length = 10
  Length2 = 10
  Profile = -> Binder005
  Refine = true
  Suppressed = false
  Type = 0
FEATURE [PartDesign::Body] Body001
  AllowCompound = false
  Group = -> [Binder004,Binder005,Pad001,Pad002]
  Origin = -> Origin001
  Tip = -> Pad002
FEATURE [App::Link] Link  label="Populate modules_placement_x with module_dropper"
  LinkedObject = -> <external composit_stand3_dropper_fix_main.FCStd>#Populate
FEATURE [Part::FeaturePython] Mirror  label="Mirror of Populate modules_placement_x with module_dropper"  # WARN: FeaturePython — macro-defined, semantics opaque (R4)
  ExposePlacement = false
  FlipX = false
  FlipY = true
  FlipZ = false
  MarkerShape = 1
  MarkerSize = 0
  NumElements = 4
  Object = -> Link
  ObjectTraversal = 0
  Type = lattice2Mirror.LatticeMirror
  isLattice = 1
FEATURE [Part::FeaturePython] Join  # WARN: FeaturePython — macro-defined, semantics opaque (R4)
  ExposePlacement = false
  Interleave = false
  Links = -> [Link,Mirror]
  MarkerShape = 1
  MarkerSize = 0
  NumElements = 8
  Type = lattice2JoinArrays.JoinArrays
  isLattice = 1
FEATURE [Part::FeaturePython] Populate  label="Populate Join with Body001"  # WARN: FeaturePython — macro-defined, semantics opaque (R4)
  Copying = 0
  ExposePlacement = false
  MarkerShape = 1
  MarkerSize = 0
  NumElements = 0
  Object = -> Body001
  OutputCompounding = 1
  PlacementsTo = -> Join
  Referencing = 0
  Type = lattice2PopulateCopies.LatticePopulateCopies
  isLattice = 0
FEATURE [App::Link] Link001  label="fix"
  LinkedObject = -> <external composit_stand3_dropper_fix_main.FCStd>#Join
FEATURE [App::Link] Link002  label="hole_3.4mm"
  LinkedObject = -> <external composit_stand3_main.FCStd>#Cylinder
FEATURE [Part::FeaturePython] Placment  label="top"  # WARN: FeaturePython — macro-defined, semantics opaque (R4)
  AttacherType = Attacher::AttachEngine3D
  ExposePlacement = true
  MarkerShape = 1
  MarkerSize = 20
  NumElements = 1
  Placement = pos=(0,0,6) rot=(1,0,0;3.14159rad)
  Type = lattice2AttachablePlacement.AttachablePlacement
  isLattice = 1
FEATURE [Part::FeaturePython] Populate002  label="Populate Placment with fix"  # WARN: FeaturePython — macro-defined, semantics opaque (R4)
  Copying = 0
  ExposePlacement = false
  MarkerShape = 1
  MarkerSize = 0
  NumElements = 5
  Object = -> Link001
  OutputCompounding = 0
  PlacementsTo = -> Placment
  Referencing = 0
  Type = lattice2PopulateCopies.LatticePopulateCopies
  isLattice = 1
FEATURE [Part::FeaturePython] Populate001  label="Populate fix with hole_3.4mm"  # WARN: FeaturePython — macro-defined, semantics opaque (R4)
  Copying = 0
  ExposePlacement = false
  MarkerShape = 1
  MarkerSize = 0
  NumElements = 0
  Object = -> Link002
  OutputCompounding = 1
  PlacementsTo = -> Populate002
  Referencing = 0
  Type = lattice2PopulateCopies.LatticePopulateCopies
  isLattice = 0
FEATURE [App::Link] Link003  label="feed_hole"
  LinkTransform = true
  LinkedObject = -> <external composit_stand3_dropper_fix_main.FCStd>#Cylinder
FEATURE [Part::FeaturePython] Populate003  label="Populate top with feed_hole"  # WARN: FeaturePython — macro-defined, semantics opaque (R4)
  Copying = 0
  ExposePlacement = false
  MarkerShape = 1
  MarkerSize = 0
  NumElements = 0
  Object = -> Link003
  OutputCompounding = 2
  PlacementsTo = -> Placment
  Referencing = 0
  Type = lattice2PopulateCopies.LatticePopulateCopies
  isLattice = 0
FEATURE [Part::MultiFuse] Fusion
  Shapes = -> [Populate,Populate001,Populate003]
FEATURE [PartDesign::Boolean] Boolean
  BaseFeature = -> Pad
  Group = -> [Fusion]
  Suppressed = false
  Type = 1
  UsePlacement = true
FEATURE [PartDesign::CoordinateSystem] Local_CS  label="dropper_fix_bottom_LCS"
  AttacherType = Attacher::AttachEngine3D
  AttachmentSupport = -> [XY_Plane]
  MapMode = 5
FEATURE [PartDesign::Body] Body  label="dropper_fix_bottom"
  AllowCompound = false
  Group = -> [Binder001,Pad,Boolean,Local_CS]
  Origin = -> Origin
  Tip = -> Boolean
FEATURE [Part::Feature] Body166  label="dropper_fix_bottom001"
  Placement = pos=(0,0,0) rot=(0,0,-1;1.5708rad)
  shape: bbox 345.1 x 84.2 x 3 mm, 100 faces (baked)
FEATURE [Part::Feature] Body167  label="dropper_fix_top001"
  shape: bbox 84.2 x 342.1 x 3 mm, 109 faces (baked)
---- part composit_stand3_dropper_fix_cap_inner_model.FCStd = doc fcstd_a1d9173eb1c9 ----
FCSTD DOCUMENT  (FreeCAD 1.1R38827 (Git))
Label: composit_stand3_dropper_fix_cap_inner_model
License: All rights reserved
LicenseURL: http://en.wikipedia.org/wiki/All_rights_reserved
objects: PartDesign::SubShapeBinder×3, App::Link×3, Part::FeaturePython×3, PartDesign::Body×3, Sketcher::SketchObject×2, PartDesign::FeaturePython×2, Part::MultiFuse×2, PartDesign::Boolean×2, PartDesign::CoordinateSystem×2, Part::Cylinder×1, Part::Mirroring×1
note: 27 computed .brp shape members not serialized (recipe doc carries the construction recipe); baked Part::Feature solids carry a one-line shape summary decoded from their .brp
EXTERNAL_REF file=composit_stand3_dropper_fix_cap_outer_main.FCStd obj=Spreadsheet
EXTERNAL_REF file=composit_stand3_dropper_fix_main.FCStd obj=Sketch
EXTERNAL_REF file=composit_stand3_dropper_fix_cap_outer_main.FCStd obj=Join
EXTERNAL_REF file=composit_stand3_dropper_fix_cap_outer_main.FCStd obj=Join001
EXTERNAL_REF file=composit_stand3_main.FCStd obj=Cylinder001
EXTERNAL_REF file=composit_stand3_dropper_fix_cap_outer_main.FCStd obj=Sketch

FEATURE [Sketcher::SketchObject] Sketch
  ArcFitTolerance = 0
  FullyConstrained = true
  MakeInternals = false
  expr: Constraints[10] = <<composit_stand3_dropper_fix_cap_outer_main>>#<<Properties>>.height - 3 mm
  expr: Constraints[11] = <<composit_stand3_dropper_fix_main>>#<<main_sketch>>.Constraints.width
  sketch-geometry (6):
    g0: LineSegment [constr] StartX=6 StartY=42.1 StartZ=0 EndX=6 EndY=-42.1 EndZ=0
    g1: LineSegment StartX=6 StartY=-42.1 StartZ=0 EndX=37 EndY=-42.1 EndZ=0
    g2: LineSegment StartX=37 StartY=-42.1 StartZ=0 EndX=37 EndY=42.1 EndZ=0
    g3: LineSegment StartX=37 StartY=42.1 StartZ=0 EndX=6 EndY=42.1 EndZ=0
    g4: GeomPoint [constr] X=21.5 Y=0 Z=0
    g5: LineSegment [constr] StartX=0 StartY=0 StartZ=0 EndX=6 EndY=4e-16 EndZ=0
  constraints (15):
    c: Coincident(g0,g1)
    c: Coincident(g1,g2)
    c: Coincident(g2,g3)
    c: Coincident(g3,g0)
    c: Symmetric(g2,g0,g4)
    c: Parallel(g2,g0)
    c: Parallel(g3,g1)
    c: Perpendicular(g3,g0)
    c: Coincident(g5,g-1)
    c: Symmetric(g0,g0,g5)
    c: Distance(g5,g2) = 37
    c: Distance(g2) = 84.2
    c: Perpendicular(g0,g5)
    c: Distance(g5) = 6
    c: PointOnObject(g4,g-1)
FEATURE [PartDesign::SubShapeBinder] Binder
  BindCopyOnChange = 0
  BindMode = 0
  ClaimChildren = true
  Context = -> Body [Binder.]
  Fuse = false
  MakeFace = true
  OffsetFill = false
  OffsetIntersection = false
  OffsetJoinType = 0
  OffsetOpenResult = false
  PartialLoad = false
  Placement = pos=(30,0,0) rot=(0,-1,0;1.5708rad)
  Relative = true
  Support = -> [Sketch]
  _Version = 2
FEATURE [PartDesign::SubShapeBinder] Binder001
  BindCopyOnChange = 0
  BindMode = 0
  ClaimChildren = false
  Context = -> Body001 [Binder001.]
  Fuse = false
  MakeFace = true
  OffsetFill = false
  OffsetIntersection = false
  OffsetJoinType = 0
  OffsetOpenResult = false
  PartialLoad = false
  Placement = pos=(0,0,37) rot=(0,0,1;0rad)
  Relative = true
  Support = -> [Connect]
  _Version = 2
  expr: .Placement.Base.z = <<composit_stand3_dropper_fix_cap_outer_main>>#<<Properties>>.height - 3 mm
  expr: Support = <<Connect>>._self
FEATURE [App::Link] Link  label="holes_3.4mm_placements"
  LinkClaimChild = true
  LinkTransform = true
  LinkedObject = -> <external composit_stand3_dropper_fix_cap_outer_main.FCStd>#Join
FEATURE [App::Link] Link001  label="holes_4mm_placements"
  LinkClaimChild = true
  LinkTransform = true
  LinkedObject = -> <external composit_stand3_dropper_fix_cap_outer_main.FCStd>#Join001
FEATURE [PartDesign::FeaturePython] BaseBend  # WARN: FeaturePython — macro-defined, semantics opaque (R4)
  BendSide = 1
  BendSketch = -> Binder
  MidPlane = false
  Reverse = true
  Suppressed = false
  length = 30
  radius = 0.1
  thickness = 0.3
FEATURE [App::Link] Link002  label="hole_3.4mm_rev"
  LinkClaimChild = true
  LinkTransform = true
  LinkedObject = -> <external composit_stand3_main.FCStd>#Cylinder001
FEATURE [Part::Cylinder] Cylinder  label="hole_4mm_rev"
  Angle = 360
  AttacherType = Attacher::AttachEngine3D
  FirstAngle = 0
  Height = 10
  Placement = pos=(0,0,0) rot=(1,0,0;3.14159rad)
  Radius = 2
  SecondAngle = 0
FEATURE [Part::FeaturePython] Populate  label="Populate holes_4mm_placements with hole_4mm_rev"  # WARN: FeaturePython — macro-defined, semantics opaque (R4)
  Copying = 0
  ExposePlacement = false
  MarkerShape = 1
  MarkerSize = 0
  NumElements = 0
  Object = -> Cylinder
  OutputCompounding = 1
  PlacementsTo = -> Link001
  Referencing = 0
  Type = lattice2PopulateCopies.LatticePopulateCopies
  isLattice = 0
FEATURE [Part::FeaturePython] Populate001  label="Populate holes_3.4mm_placements with hole_3.4mm_rev"  # WARN: FeaturePython — macro-defined, semantics opaque (R4)
  Copying = 0
  ExposePlacement = false
  MarkerShape = 1
  MarkerSize = 0
  NumElements = 0
  Object = -> Link002
  OutputCompounding = 1
  PlacementsTo = -> Link
  Referencing = 0
  Type = lattice2PopulateCopies.LatticePopulateCopies
  isLattice = 0
FEATURE [PartDesign::Body] Body002
  AllowCompound = false
  Origin = -> Origin002
FEATURE [Part::MultiFuse] Fusion
  Shapes = -> [Populate,Populate001]
FEATURE [PartDesign::Boolean] Boolean
  BaseFeature = -> BaseBend
  Group = -> [Fusion]
  Suppressed = false
  Type = 1
  UsePlacement = true
FEATURE [Part::MultiFuse] Fusion001
  Shapes = -> [Populate,Populate001]
FEATURE [PartDesign::FeaturePython] BaseBend001  # WARN: FeaturePython — macro-defined, semantics opaque (R4)
  BendSide = 0
  BendSketch = -> Binder001
  MidPlane = false
  Reverse = true
  Suppressed = false
  length = 70
  radius = 0.1
  thickness = 0.3
FEATURE [PartDesign::Boolean] Boolean001
  BaseFeature = -> BaseBend001
  Group = -> [Fusion001]
  Suppressed = false
  Type = 1
  UsePlacement = true
FEATURE [PartDesign::CoordinateSystem] Local_CS
  AttacherType = Attacher::AttachEngine3D
  AttachmentSupport = -> [XY_Plane]
  MapMode = 5
FEATURE [PartDesign::Body] Body  label="cap_inner_1"
  AllowCompound = false
  Group = -> [Binder,BaseBend,Boolean,Local_CS]
  Origin = -> Origin
  Tip = -> Boolean
FEATURE [PartDesign::CoordinateSystem] Local_CS001
  AttacherType = Attacher::AttachEngine3D
  AttachmentSupport = -> [XY_Plane001]
  MapMode = 5
FEATURE [PartDesign::Body] Body001  label="cap_inner_2"
  AllowCompound = false
  Group = -> [Binder001,BaseBend001,Boolean001,Local_CS001]
  Origin = -> Origin001
  Tip = -> Boolean001
FEATURE [PartDesign::SubShapeBinder] Binder002
  BindCopyOnChange = 0
  BindMode = 0
  ClaimChildren = false
  Fuse = false
  MakeFace = true
  OffsetFill = false
  OffsetIntersection = false
  OffsetJoinType = 0
  OffsetOpenResult = false
  PartialLoad = false
  Relative = true
  Support = -> [<external composit_stand3_dropper_fix_cap_outer_main.FCStd>#Sketch]
  _Version = 2
  expr: Support = composit_stand3_dropper_fix_cap_outer_main#<<main_sketch>>._self
FEATURE [Sketcher::SketchObject] Sketch001
  ArcFitTolerance = 0
  ExternalGeometry = -> [Binder002]
  FullyConstrained = true
  MakeInternals = false
  sketch-geometry (7):
    g0: LineSegment StartX=270.046 StartY=0 StartZ=0 EndX=270.046 EndY=42.1 EndZ=0
    g1: LineSegment StartX=270.046 StartY=42.1 StartZ=0 EndX=292.046 EndY=42.1 EndZ=0
    g2: LineSegment StartX=292.046 StartY=42.1 StartZ=0 EndX=348.872 EndY=14.5 EndZ=0
    g3: LineSegment StartX=348.872 StartY=14.5 StartZ=0 EndX=348.872 EndY=0 EndZ=0
    g4: LineSegment [constr] StartX=292.046 StartY=45.1 StartZ=0 EndX=292.046 EndY=42.1 EndZ=0
    g5: LineSegment [constr] StartX=292.046 StartY=42.1 StartZ=0 EndX=293.356 EndY=44.7985 EndZ=0
    g6: LineSegment [constr] StartX=348.872 StartY=14.5 StartZ=0 EndX=351.872 EndY=14.5 EndZ=0
  constraints (22):
    c: PointOnObject(g0,g-1)
    c: Vertical(g0)
    c: Coincident(g0,g1)
    c: Horizontal(g1)
    c: Coincident(g1,g2)
    c: Coincident(g2,g3)
    c: PointOnObject(g3,g-1)
    c: Vertical(g3)
    c: Coincident(g4,g1)
    c: Vertical(g4)
    c: Coincident(g4,g5)
    c: PointOnObject(g5,g-3)
    c: Coincident(g2,g6)
    c: Horizontal(g6)
    c: Vertical(g-3,g6)
    c: Perpendicular(g-3,g5)
    c: Horizontal(g4,g-3)
    c: Equal(g4,g5)
    c: Equal(g5,g6)
    c: DistanceY(g4,g4) = 3
    c: DistanceX(g1,g1) = 22
    c: Perpendicular(g5,g2)
FEATURE [Part::Mirroring] Part__Mirroring  label="Sketch001 (Mirror #1)"
  Base = (0,0,0)
  Normal = (0,1,0)
  Source = -> Sketch001
FEATURE [Part::FeaturePython] Connect  # WARN: FeaturePython — macro-defined, semantics opaque (R4)
  Objects = -> [Sketch001,Part__Mirroring]
  Tolerance = 0
---- part composit_stand3_dropper_fix_cap_outer_model.FCStd = doc fcstd_8576de4b6be2 ----
FCSTD DOCUMENT  (FreeCAD 1.1R38827 (Git))
Label: composit_stand3_dropper_fix_cap_outer_model
License: All rights reserved
LicenseURL: http://en.wikipedia.org/wiki/All_rights_reserved
objects: Part::FeaturePython×5, PartDesign::SubShapeBinder×4, Part::Mirroring×4, PartDesign::FeaturePython×3, App::Link×3, PartDesign::Body×2, Sketcher::SketchObject×2, Part::Extrusion×2, PartDesign::Pocket×1, Measure::MeasureDistance×1, App::DocumentObjectGroup×1, Part::Feature×1, Part::Cylinder×1, PartDesign::CoordinateSystem×1, Part::MultiFuse×1, PartDesign::Boolean×1
note: 36 computed .brp shape members not serialized (recipe doc carries the construction recipe); baked Part::Feature solids carry a one-line shape summary decoded from their .brp
EXTERNAL_REF file=composit_stand3_dropper_fix_cap_outer_main.FCStd obj=Sketch
EXTERNAL_REF file=composit_stand3_dropper_fix_cap_outer_main.FCStd obj=Sketch002
EXTERNAL_REF file=composit_stand3_dropper_fix_cap_outer_main.FCStd obj=Spreadsheet
EXTERNAL_REF file=composit_stand3_dropper_fix_cap_outer_main.FCStd obj=Join
EXTERNAL_REF file=composit_stand3_dropper_fix_cap_outer_main.FCStd obj=Join001
EXTERNAL_REF file=composit_stand3_main.FCStd obj=Cylinder001

FEATURE [PartDesign::SubShapeBinder] Binder
  BindCopyOnChange = 0
  BindMode = 0
  ClaimChildren = true
  Fuse = false
  MakeFace = true
  OffsetFill = false
  OffsetIntersection = false
  OffsetJoinType = 0
  OffsetOpenResult = false
  PartialLoad = false
  Relative = false
  Support = -> [<external composit_stand3_dropper_fix_cap_outer_main.FCStd>#Sketch]
  _Version = 2
FEATURE [Part::Mirroring] Part__Mirroring  label="Binder (Mirror #1)"
  Base = (0,0,0)
  Normal = (0,1,0)
  Source = -> Binder
FEATURE [Part::FeaturePython] Connect  # WARN: FeaturePython — macro-defined, semantics opaque (R4)
  Objects = -> [Binder,Part__Mirroring]
  Tolerance = 0
FEATURE [PartDesign::SubShapeBinder] Binder001
  BindCopyOnChange = 0
  BindMode = 0
  ClaimChildren = true
  Context = -> Body [Binder001.]
  Fuse = false
  MakeFace = true
  OffsetFill = false
  OffsetIntersection = false
  OffsetJoinType = 0
  OffsetOpenResult = false
  PartialLoad = false
  Relative = false
  Support = -> [Connect]
  _Version = 2
FEATURE [PartDesign::Body] Body001
  AllowCompound = false
  Origin = -> Origin001
FEATURE [PartDesign::SubShapeBinder] Binder002
  BindCopyOnChange = 0
  BindMode = 0
  ClaimChildren = true
  Fuse = false
  MakeFace = true
  OffsetFill = false
  OffsetIntersection = false
  OffsetJoinType = 0
  OffsetOpenResult = false
  PartialLoad = false
  Relative = false
  Support = -> [<external composit_stand3_dropper_fix_cap_outer_main.FCStd>#Sketch002]
  _Version = 2
FEATURE [Part::Mirroring] Part__Mirroring001  label="Binder002 (Mirror #2)"
  Base = (0,0,0)
  Normal = (0,1,0)
  Source = -> Binder002
FEATURE [Part::FeaturePython] Connect001  # WARN: FeaturePython — macro-defined, semantics opaque (R4)
  Objects = -> [Binder002,Part__Mirroring001]
  Tolerance = 0
FEATURE [PartDesign::SubShapeBinder] Binder003
  BindCopyOnChange = 0
  BindMode = 0
  ClaimChildren = false
  Context = -> Body [Binder003.]
  Fuse = false
  MakeFace = true
  OffsetFill = false
  OffsetIntersection = false
  OffsetJoinType = 0
  OffsetOpenResult = false
  PartialLoad = false
  Placement = pos=(0,0,39.6) rot=(0,0,1;0rad)
  Relative = true
  Support = -> [Connect001]
  _Version = 2
  expr: .Placement.Base.z = <<BaseBend>>.length
FEATURE [PartDesign::FeaturePython] BaseBend  # WARN: FeaturePython — macro-defined, semantics opaque (R4)
  BendSide = 1
  BendSketch = -> Binder001
  MidPlane = false
  Reverse = false
  Suppressed = false
  length = 39.6
  radius = 0.1
  thickness = 0.3
  expr: length = <<composit_stand3_dropper_fix_cap_outer_main>>#<<Properties>>.height - radius - thickness
FEATURE [PartDesign::FeaturePython] Extend  # WARN: FeaturePython — macro-defined, semantics opaque (R4)
  BaseFeature = -> BaseBend
  Offset = 0.02
  Refine = true
  Suppressed = false
  UseSubtraction = false
  baseObject = -> BaseBend [Face1]
  gap1 = 0
  gap2 = 0
  length = 0
FEATURE [PartDesign::FeaturePython] Bend  # WARN: FeaturePython — macro-defined, semantics opaque (R4)
  AutoMiter = false
  BaseFeature = -> Extend
  BendType = 0
  LengthList = [45.1]
  LengthSpec = 1
  NonperforationMaxLength = 5
  Perforate = false
  PerforationAngle = 0
  PerforationInitialLength = 5
  PerforationMaxLength = 5
  ReliefFactor = 0.7
  Suppressed = false
  UseReliefFactor = false
  angle = 90
  baseObject = -> Extend [Edge4,Edge17,Edge33,Edge107,Edge62,Edge79,Edge95]
  bendAList = [90]
  extend1 = 0
  extend2 = 0
  gap1 = 0
  gap2 = 0
  invert = false
  kfactor = 0.5
  length = 45.1
  maxExtendDist = 5
  minGap = 0.2
  minReliefGap = 1
  miterangle1 = 0
  miterangle2 = 0
  offset = 0
  radius = 0.1
  reliefType = 0
  reliefd = 1
  reliefw = 0.8
  sketchflip = false
  sketchinvert = false
  unfold = false
  expr: radius = BaseBend.radius
FEATURE [PartDesign::Pocket] Pocket
  BaseFeature = -> Bend
  Direction = (0,0,-1)
  Length = 5
  Length2 = 5
  Profile = -> Binder003
  Refine = true
  Reversed = true
  Suppressed = false
  Type = 0
FEATURE [Measure::MeasureDistance] Distance  label="Distance: 281,5882 mm"
  Distance = 281.588
  DistanceX = 281.588
  DistanceY = 0
  DistanceZ = 2.84e-14
  Element1 = -> Pocket [Edge197]
  Element2 = -> Pocket [Edge244]
  Position1 = (282.425,-0.05,40)
  Position2 = (0.837158,-0.05,40)
FEATURE [App::DocumentObjectGroup] Measurements
  Group = -> [Distance]
FEATURE [Part::Feature] Body168  label="cap_outer_material_0.30ansi002"
  Placement = pos=(0,0,0) rot=(0,0,-1;1.5708rad)
  shape: bbox 339.9 x 90.2 x 40.4 mm, 133 faces (baked)
FEATURE [App::Link] Link  label="holes_3.4mm_placements"
  LinkClaimChild = true
  LinkTransform = true
  LinkedObject = -> <external composit_stand3_dropper_fix_cap_outer_main.FCStd>#Join
FEATURE [App::Link] Link001  label="holes_4mm_placements"
  LinkClaimChild = true
  LinkTransform = true
  LinkedObject = -> <external composit_stand3_dropper_fix_cap_outer_main.FCStd>#Join001
FEATURE [App::Link] Link002  label="hole_3.4mm_rev"
  LinkTransform = true
  LinkedObject = -> <external composit_stand3_main.FCStd>#Cylinder001
FEATURE [Part::Cylinder] Cylinder  label="hole_4mm_rev"
  Angle = 360
  AttacherType = Attacher::AttachEngine3D
  FirstAngle = 0
  Height = 10
  Placement = pos=(0,0,0) rot=(1,0,0;3.14159rad)
  Radius = 2
  SecondAngle = 0
FEATURE [Part::FeaturePython] Populate  label="Populate holes_3.4mm_placements with hole_3.4mm_rev"  # WARN: FeaturePython — macro-defined, semantics opaque (R4)
  Copying = 0
  ExposePlacement = false
  MarkerShape = 1
  MarkerSize = 0
  NumElements = 0
  Object = -> Link002
  OutputCompounding = 1
  PlacementsTo = -> Link
  Referencing = 0
  Type = lattice2PopulateCopies.LatticePopulateCopies
  isLattice = 0
FEATURE [Part::FeaturePython] Populate001  label="Populate holes_4mm_placements with hole_4mm_rev"  # WARN: FeaturePython — macro-defined, semantics opaque (R4)
  Copying = 0
  ExposePlacement = false
  MarkerShape = 1
  MarkerSize = 0
  NumElements = 0
  Object = -> Cylinder
  OutputCompounding = 1
  PlacementsTo = -> Link001
  Referencing = 0
  Type = lattice2PopulateCopies.LatticePopulateCopies
  isLattice = 0
FEATURE [Sketcher::SketchObject] Sketch
  ArcFitTolerance = 0
  ExternalGeometry = -> [Body168,Connect]
  FullyConstrained = true
  MakeInternals = false
  sketch-geometry (5):
    g0: ArcOfCircle CenterX=0 CenterY=0 CenterZ=0 NormalX=0 NormalY=0 NormalZ=1 AngleXU=0 Radius=21.5 StartAngle=0 EndAngle=0.907973
    g1: ArcOfCircle CenterX=15.076 CenterY=19.3123 CenterZ=0 NormalX=0 NormalY=0 NormalZ=1 AngleXU=0 Radius=3 StartAngle=2.61799 EndAngle=4.04957
    g2: LineSegment StartX=12.4779 StartY=20.8123 StartZ=0 EndX=18.471 EndY=31.1927 EndZ=0
    g3: LineSegment StartX=18.471 StartY=31.1927 StartZ=0 EndX=18.1246 EndY=31.3927 EndZ=0
    g4: LineSegment StartX=18.1246 StartY=31.3927 StartZ=0 EndX=0 EndY=0 EndZ=0
  constraints (14):
    c: Coincident(g0,g-1)
    c: PointOnObject(g0,g-1)
    c: Tangent(g1,g0) = 1.5708
    c: Radius(g0) = 21.5
    c: Radius(g1) = 3
    c: Tangent(g1,g2) = 1.5708
    c: Coincident(g2,g3)
    c: Coincident(g3,g4)
    c: Coincident(g4,g0)
    c: Perpendicular(g3,g4)
    c: Perpendicular(g2,g3)
    c: Angle(g4) = -2.0944
    c: Distance(g4) = 36.2492
    c: Distance(g3) = 0.4
FEATURE [Part::Mirroring] Part__Mirroring002  label="Sketch (Mirror #3)"
  Base = (0,0,0)
  Normal = (0,1,0)
  Source = -> Sketch
FEATURE [Part::FeaturePython] Connect002  # WARN: FeaturePython — macro-defined, semantics opaque (R4)
  Objects = -> [Sketch,Part__Mirroring002]
  Tolerance = 0
FEATURE [Part::Extrusion] Extrude
  Base = -> Connect002
  Dir = (0,0,1)
  DirMode = 2
  FaceMakerClass = Part::FaceMakerBullseye
  FaceMakerMode = 3
  LengthFwd = 40
  LengthRev = 0
  Solid = true
  Symmetric = false
  expr: LengthFwd = <<composit_stand3_dropper_fix_cap_outer_main>>#<<Properties>>.height
FEATURE [PartDesign::CoordinateSystem] Local_CS
  AttacherType = Attacher::AttachEngine3D
  AttachmentSupport = -> [XY_Plane]
  MapMode = 5
FEATURE [Sketcher::SketchObject] Sketch001
  ArcFitTolerance = 0
  AttachmentOffset = pos=(0,0,0) rot=(0,-1,0;1.5708rad)
  AttachmentSupport = -> [Sketch]
  FullyConstrained = true
  MakeInternals = false
  MapMode = 7
  Placement = pos=(18.1246,31.3927,0) rot=(0.774597,0.447214,0.447214;1.82348rad)
  sketch-geometry (3):
    g0: LineSegment StartX=0 StartY=0 StartZ=0 EndX=3 EndY=1.865e-13 EndZ=0
    g1: LineSegment StartX=0 StartY=0 StartZ=0 EndX=1.865e-13 EndY=3 EndZ=0
    g2: ArcOfCircle CenterX=3 CenterY=3 CenterZ=0 NormalX=0 NormalY=0 NormalZ=1 AngleXU=0 Radius=3 StartAngle=3.14159 EndAngle=4.71239
  constraints (7):
    c: Coincident(g-1,g0)
    c: PointOnObject(g0,g-1)
    c: Coincident(g0,g1)
    c: PointOnObject(g1,g-2)
    c: Tangent(g2,g1) = 1.5708
    c: Tangent(g2,g0) = -1.5708
    c: Radius(g2) = 3
FEATURE [Part::Extrusion] Extrude001
  Base = -> Sketch001
  Dir = (0.866025,-0.5,1e-16)
  DirMode = 2
  FaceMakerClass = Part::FaceMakerBullseye
  FaceMakerMode = 3
  LengthFwd = 10
  LengthRev = 0
  Solid = true
  Symmetric = false
FEATURE [Part::Mirroring] Part__Mirroring003  label="Extrude001 (Mirror #4)"
  Base = (0,0,0)
  Normal = (0,1,0)
  Source = -> Extrude001
FEATURE [Part::MultiFuse] Fusion
  Shapes = -> [Populate,Populate001,Extrude,Extrude001,Part__Mirroring003]
FEATURE [PartDesign::Boolean] Boolean
  BaseFeature = -> Pocket
  Group = -> [Fusion]
  Suppressed = false
  Type = 1
  UsePlacement = true
FEATURE [PartDesign::Body] Body  label="cap_outer_dropper_fix"
  AllowCompound = false
  Group = -> [Binder001,Binder003,BaseBend,Extend,Bend,Pocket,Boolean,Local_CS]
  Origin = -> Origin
  Tip = -> Boolean
---- part composit_stand3_dropper_fix_fixture_model.FCStd = doc fcstd_42cb5ebbac59 ----
FCSTD DOCUMENT  (FreeCAD 1.1R38827 (Git))
Label: composit_stand3_dropper_fix_fixture_model
License: All rights reserved
LicenseURL: http://en.wikipedia.org/wiki/All_rights_reserved
objects: App::Link×4, Part::FeaturePython×3, PartDesign::SubShapeBinder×2, PartDesign::Body×2, PartDesign::FeaturePython×1, Part::MultiFuse×1, PartDesign::Boolean×1, PartDesign::CoordinateSystem×1
note: 13 computed .brp shape members not serialized (recipe doc carries the construction recipe); baked Part::Feature solids carry a one-line shape summary decoded from their .brp
EXTERNAL_REF file=composit_stand3_dropper_fix_fixture_main.FCStd obj=Sketch
EXTERNAL_REF file=composit_stand3_dropper_fix_fixture_main.FCStd obj=Placment
EXTERNAL_REF file=composit_stand3_main.FCStd obj=Cylinder
EXTERNAL_REF file=composit_stand3_dropper_fix_fixture_main.FCStd obj=Join
EXTERNAL_REF file=composit_stand3_dropper_fix_main.FCStd obj=Join

FEATURE [PartDesign::SubShapeBinder] Binder
  BindCopyOnChange = 0
  BindMode = 0
  ClaimChildren = true
  Fuse = false
  MakeFace = true
  OffsetFill = false
  OffsetIntersection = false
  OffsetJoinType = 0
  OffsetOpenResult = false
  PartialLoad = false
  Placement = pos=(0,0,0) rot=(0.57735,0.57735,0.57735;2.0944rad)
  Relative = false
  Support = -> [<external composit_stand3_dropper_fix_fixture_main.FCStd>#Sketch]
  _Version = 2
  expr: Placement = Support[0][0].Placement
FEATURE [PartDesign::SubShapeBinder] Binder001
  BindCopyOnChange = 0
  BindMode = 0
  ClaimChildren = true
  Context = -> Body [Binder001.]
  Fuse = false
  MakeFace = true
  OffsetFill = false
  OffsetIntersection = false
  OffsetJoinType = 0
  OffsetOpenResult = false
  PartialLoad = false
  Placement = pos=(0,0,0) rot=(0.57735,0.57735,0.57735;2.0944rad)
  Relative = false
  Support = -> [Binder]
  _Version = 2
  expr: Placement = Support[0][0].Placement
FEATURE [PartDesign::FeaturePython] BaseBend  # WARN: FeaturePython — macro-defined, semantics opaque (R4)
  BendSide = 1
  BendSketch = -> Binder001
  MidPlane = false
  Reverse = false
  Suppressed = false
  length = 100
  radius = 0.1
  thickness = 0.3
FEATURE [App::Link] Link  label="Placment"
  LinkTransform = true
  LinkedObject = -> <external composit_stand3_dropper_fix_fixture_main.FCStd>#Placment
FEATURE [App::Link] Link001  label="hole_3.4mm"
  LinkedObject = -> <external composit_stand3_main.FCStd>#Cylinder
FEATURE [App::Link] Link002  label="Join"
  LinkedObject = -> <external composit_stand3_dropper_fix_fixture_main.FCStd>#Join
FEATURE [PartDesign::Body] Body001
  AllowCompound = false
  Origin = -> Origin001
FEATURE [App::Link] Link003  label="fix"
  LinkedObject = -> <external composit_stand3_dropper_fix_main.FCStd>#Join
FEATURE [Part::FeaturePython] Populate001  label="Populate Placment with fix"  # WARN: FeaturePython — macro-defined, semantics opaque (R4)
  Copying = 0
  ExposePlacement = false
  MarkerShape = 1
  MarkerSize = 0
  NumElements = 5
  Object = -> Link003
  OutputCompounding = 0
  PlacementsTo = -> Link
  Referencing = 0
  Type = lattice2PopulateCopies.LatticePopulateCopies
  isLattice = 1
FEATURE [Part::FeaturePython] Join  label="Join001"  # WARN: FeaturePython — macro-defined, semantics opaque (R4)
  ExposePlacement = false
  Interleave = false
  Links = -> [Link002,Populate001]
  MarkerShape = 1
  MarkerSize = 0
  NumElements = 15
  Type = lattice2JoinArrays.JoinArrays
  isLattice = 1
FEATURE [Part::FeaturePython] Populate  label="Populate Join with hole_3.4mm"  # WARN: FeaturePython — macro-defined, semantics opaque (R4)
  Copying = 0
  ExposePlacement = false
  MarkerShape = 1
  MarkerSize = 0
  NumElements = 0
  Object = -> Link001
  OutputCompounding = 1
  PlacementsTo = -> Join
  Referencing = 0
  Type = lattice2PopulateCopies.LatticePopulateCopies
  isLattice = 0
FEATURE [Part::MultiFuse] Fusion
  Shapes = -> [Populate]
FEATURE [PartDesign::Boolean] Boolean
  BaseFeature = -> BaseBend
  Group = -> [Fusion]
  Suppressed = false
  Type = 1
  UsePlacement = true
FEATURE [PartDesign::CoordinateSystem] Local_CS
  AttacherType = Attacher::AttachEngine3D
  AttachmentOffset = pos=(-50,0,0) rot=(0,0,1;0rad)
  AttachmentSupport = -> [XY_Plane]
  MapMode = 5
  Placement = pos=(-50,0,0) rot=(0,0,1;0rad)
  expr: .AttachmentOffset.Base.x = <<Placment>>.LinkedObject.Placement.Base.x
FEATURE [PartDesign::Body] Body  label="dropper_fix_fixture"
  AllowCompound = false
  Group = -> [Binder001,BaseBend,Boolean,Local_CS]
  Origin = -> Origin
  Tip = -> Boolean
---- part composit_stand3_dropper_fix_top_model.FCStd = doc fcstd_5f1bdb20550e ----
FCSTD DOCUMENT  (FreeCAD 1.1R38827 (Git))
Label: composit_stand3_dropper_fix_top_model
License: All rights reserved
LicenseURL: http://en.wikipedia.org/wiki/All_rights_reserved
objects: PartDesign::SubShapeBinder×7, Part::FeaturePython×6, App::Link×4, PartDesign::Pad×3, PartDesign::Body×2, Part::Mirroring×1, Part::Compound×1, Part::MultiFuse×1, PartDesign::Boolean×1, PartDesign::CoordinateSystem×1
note: 30 computed .brp shape members not serialized (recipe doc carries the construction recipe); baked Part::Feature solids carry a one-line shape summary decoded from their .brp
EXTERNAL_REF file=composit_stand3_dropper_fix_main.FCStd obj=Sketch
EXTERNAL_REF file=../dropper.FCStd obj=Sketch007
EXTERNAL_REF file=../dropper.FCStd obj=Part
EXTERNAL_REF file=composit_stand3_dropper_fix_main.FCStd obj=Populate
EXTERNAL_REF file=composit_stand3_dropper_fix_main.FCStd obj=Cylinder
EXTERNAL_REF file=composit_stand3_dropper_fix_main.FCStd obj=Join
EXTERNAL_REF file=composit_stand3_main.FCStd obj=Cylinder

FEATURE [PartDesign::SubShapeBinder] Binder
  BindCopyOnChange = 0
  BindMode = 0
  ClaimChildren = true
  Fuse = false
  MakeFace = true
  OffsetFill = false
  OffsetIntersection = false
  OffsetJoinType = 0
  OffsetOpenResult = false
  PartialLoad = false
  Relative = false
  Support = -> [<external composit_stand3_dropper_fix_main.FCStd>#Sketch]
  _Version = 2
FEATURE [Part::Mirroring] Part__Mirroring  label="Binder (Mirror #1)"
  Base = (0,0,0)
  Normal = (0,1,0)
  Source = -> Binder
FEATURE [Part::FeaturePython] Connect  # WARN: FeaturePython — macro-defined, semantics opaque (R4)
  Objects = -> [Binder,Part__Mirroring]
  Tolerance = 0
FEATURE [PartDesign::SubShapeBinder] Binder001
  BindCopyOnChange = 0
  BindMode = 0
  ClaimChildren = true
  Context = -> Body [Binder001.]
  Fuse = false
  MakeFace = true
  OffsetFill = false
  OffsetIntersection = false
  OffsetJoinType = 0
  OffsetOpenResult = false
  PartialLoad = false
  Relative = false
  Support = -> [Connect]
  _Version = 2
FEATURE [PartDesign::SubShapeBinder] Binder002
  BindCopyOnChange = 0
  BindMode = 0
  ClaimChildren = false
  Fuse = false
  MakeFace = true
  OffsetFill = false
  OffsetIntersection = false
  OffsetJoinType = 0
  OffsetOpenResult = false
  PartialLoad = false
  Relative = false
  Support = -> [<external ../dropper.FCStd>#Sketch007]
  _Version = 2
  expr: Support = dropper#<<base>>._self
FEATURE [PartDesign::SubShapeBinder] Binder003
  BindCopyOnChange = 0
  BindMode = 0
  ClaimChildren = false
  Fuse = false
  MakeFace = true
  OffsetFill = false
  OffsetIntersection = false
  OffsetJoinType = 0
  OffsetOpenResult = false
  PartialLoad = false
  Relative = false
  Support = -> [<external ../dropper.FCStd>#Part[Body.Binder.Connect.]]
  _Version = 2
FEATURE [PartDesign::SubShapeBinder] Binder004
  BindCopyOnChange = 0
  BindMode = 0
  ClaimChildren = false
  Fuse = false
  MakeFace = true
  OffsetFill = false
  OffsetIntersection = false
  OffsetJoinType = 0
  OffsetOpenResult = false
  PartialLoad = false
  Relative = true
  Support = -> [<external ../dropper.FCStd>#Part[Body.Sketch008.]]
  _Version = 2
FEATURE [Part::Compound] Compound
  Links = -> [Binder002,Binder003]
FEATURE [Part::FeaturePython] FuseCompound  # WARN: FeaturePython — macro-defined, semantics opaque (R4)
  Base = -> Compound
  Refine = true
  recomputeQuota = -1
FEATURE [PartDesign::SubShapeBinder] Binder005
  BindCopyOnChange = 0
  BindMode = 0
  ClaimChildren = true
  Context = -> Body001 [Binder005.]
  Fuse = false
  MakeFace = true
  OffsetFill = false
  OffsetIntersection = false
  OffsetJoinType = 0
  OffsetOpenResult = false
  PartialLoad = false
  Placement = pos=(0,0,1.5) rot=(0,0,1;0rad)
  Relative = false
  Support = -> [FuseCompound]
  _Version = 2
FEATURE [PartDesign::SubShapeBinder] Binder006
  BindCopyOnChange = 0
  BindMode = 0
  ClaimChildren = true
  Context = -> Body001 [Binder006.]
  Fuse = false
  MakeFace = true
  OffsetFill = false
  OffsetIntersection = false
  OffsetJoinType = 0
  OffsetOpenResult = false
  PartialLoad = false
  Relative = false
  Support = -> [Binder004]
  _Version = 2
FEATURE [PartDesign::Pad] Pad
  Direction = (0,0,1)
  Length = 10
  Length2 = 10
  Profile = -> Binder006
  Suppressed = false
  Type = 0
FEATURE [PartDesign::Pad] Pad001
  BaseFeature = -> Pad
  Direction = (0,0,1)
  Length = 10
  Length2 = 10
  Profile = -> Binder005
  Suppressed = false
  Type = 0
FEATURE [PartDesign::Body] Body001
  AllowCompound = false
  Group = -> [Binder005,Binder006,Pad,Pad001]
  Origin = -> Origin001
  Tip = -> Pad001
FEATURE [PartDesign::Pad] Pad002
  Direction = (0,0,1)
  Length = 3
  Length2 = 10
  Profile = -> Binder001
  Suppressed = false
  Type = 0
FEATURE [App::Link] Link  label="Populate modules_placement_x with module_dropper"
  LinkedObject = -> <external composit_stand3_dropper_fix_main.FCStd>#Populate
FEATURE [Part::FeaturePython] Mirror  label="Mirror of Populate modules_placement_x with module_dropper"  # WARN: FeaturePython — macro-defined, semantics opaque (R4)
  ExposePlacement = false
  FlipX = false
  FlipY = true
  FlipZ = false
  MarkerShape = 1
  MarkerSize = 0
  NumElements = 4
  Object = -> Link
  ObjectTraversal = 0
  Type = lattice2Mirror.LatticeMirror
  isLattice = 1
FEATURE [Part::FeaturePython] Join  # WARN: FeaturePython — macro-defined, semantics opaque (R4)
  ExposePlacement = false
  Interleave = false
  Links = -> [Link,Mirror]
  MarkerShape = 1
  MarkerSize = 0
  NumElements = 8
  Type = lattice2JoinArrays.JoinArrays
  isLattice = 1
FEATURE [Part::FeaturePython] Populate  label="Populate Join with Body001"  # WARN: FeaturePython — macro-defined, semantics opaque (R4)
  Copying = 0
  ExposePlacement = false
  MarkerShape = 1
  MarkerSize = 0
  NumElements = 0
  Object = -> Body001
  OutputCompounding = 1
  PlacementsTo = -> Join
  Referencing = 0
  Type = lattice2PopulateCopies.LatticePopulateCopies
  isLattice = 0
FEATURE [App::Link] Link001  label="feed_hole"
  LinkTransform = true
  LinkedObject = -> <external composit_stand3_dropper_fix_main.FCStd>#Cylinder
FEATURE [App::Link] Link002  label="fix"
  LinkedObject = -> <external composit_stand3_dropper_fix_main.FCStd>#Join
FEATURE [App::Link] Link003  label="hole_3.4mm"
  LinkedObject = -> <external composit_stand3_main.FCStd>#Cylinder
FEATURE [Part::FeaturePython] Populate001  label="Populate fix with hole_3.4mm"  # WARN: FeaturePython — macro-defined, semantics opaque (R4)
  Copying = 0
  ExposePlacement = false
  MarkerShape = 1
  MarkerSize = 0
  NumElements = 0
  Object = -> Link003
  OutputCompounding = 1
  PlacementsTo = -> Link002
  Referencing = 0
  Type = lattice2PopulateCopies.LatticePopulateCopies
  isLattice = 0
FEATURE [Part::MultiFuse] Fusion
  Shapes = -> [Populate,Link001,Populate001]
FEATURE [PartDesign::Boolean] Boolean
  BaseFeature = -> Pad002
  Group = -> [Fusion]
  Suppressed = false
  Type = 1
  UsePlacement = true
FEATURE [PartDesign::CoordinateSystem] Local_CS  label="dropper_fix_top_LCS"
  AttacherType = Attacher::AttachEngine3D
  AttachmentOffset = pos=(0,0,6) rot=(1,0,0;3.14159rad)
  AttachmentSupport = -> [XY_Plane]
  MapMode = 5
  Placement = pos=(0,0,6) rot=(1,0,0;3.14159rad)
FEATURE [PartDesign::Body] Body  label="dropper_fix_top"
  AllowCompound = false
  Group = -> [Binder001,Pad002,Boolean,Local_CS]
  Origin = -> Origin
  Tip = -> Boolean
